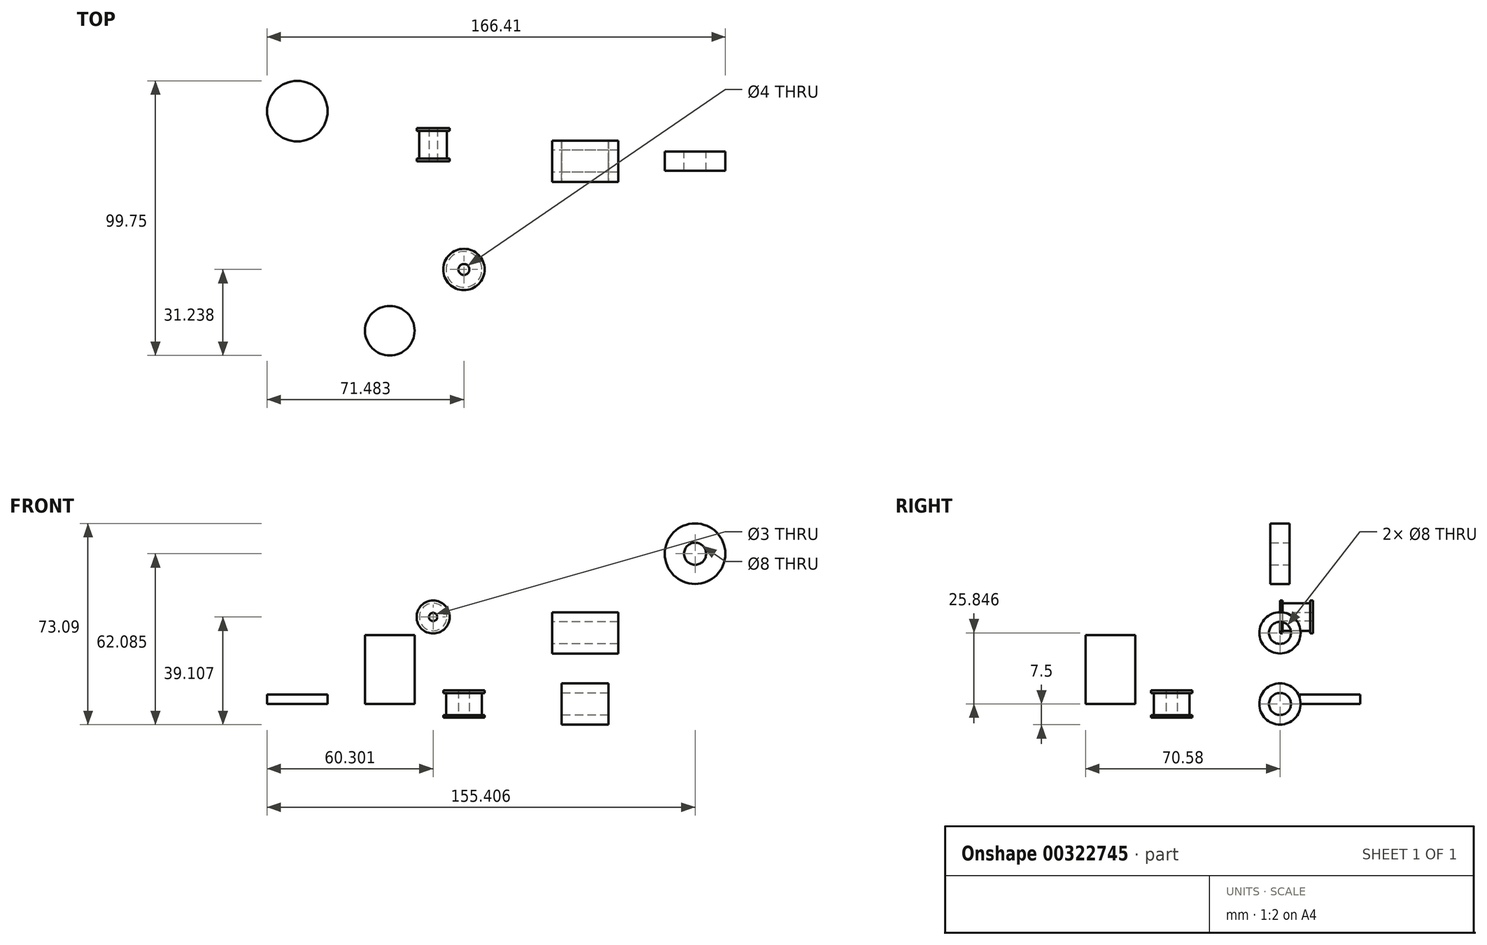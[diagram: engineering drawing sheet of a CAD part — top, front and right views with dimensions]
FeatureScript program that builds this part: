
annotation { "Feature Type Name" : "Feature", "Feature Type Description" : "" }
export const myFeature = defineFeature(function(context is Context, id is Id, definition is map)
    precondition{}
    {
        {
            var Q0;
            Q0=qCreatedBy(makeId("Right.planeOp"),FACE);
            var sketch = newSketch(context, id + "F0", { "sketchPlane" : qUnion([Q0])});
            skCircle(sketch, "E0", {"center": v(0, 0) * mm, "radius": 7.5 * mm});
            skCircle(sketch, "E1", {"center": v(0, 0) * mm, "radius": 4 * mm});
            skCircle(sketch, "E2", {"center": v(0, 25.85) * mm, "radius": 7.5 * mm});
            skCircle(sketch, "E3", {"center": v(0, 25.85) * mm, "radius": 4 * mm});
            skSolve(sketch);
        }
        {
            var Q0;
            Q0=makeQuery(id+"F0.imprint","IMPRINT",FACE,{"disambiguationData":[TD([[makeQuery(id+"F0.imprint","IMPRINT",EDGE,{"derivedFrom":sQuery(id+"F0.wireOp",EDGE,"E0")}),1.0]])]});
            extrude(context, id + "F1", {"entities" : qUnion([Q0]), "depth" : 17 * mm, "symmetric" : true});
        }
        {
            var Q0;
            Q0=makeQuery(id+"F0.imprint","IMPRINT",FACE,{"disambiguationData":[TD([[makeQuery(id+"F0.imprint","IMPRINT",EDGE,{"derivedFrom":sQuery(id+"F0.wireOp",EDGE,"E2")}),1.0]])]});
            extrude(context, id + "F2", {"entities" : qUnion([Q0]), "depth" : 24 * mm, "symmetric" : true});
        }
        {
            var Q0;
            Q0=qCreatedBy(makeId("Front.planeOp"),FACE);
            var sketch = newSketch(context, id + "F3", { "sketchPlane" : qUnion([Q0])});
            skCircle(sketch, "E4", {"center": v(-55.18, 31.6) * mm, "radius": 6 * mm});
            skCircle(sketch, "E5", {"center": v(-55.18, 31.6) * mm, "radius": 1.5 * mm});
            skSolve(sketch);
        }
        {
            var Q0;
            Q0=makeQuery(id+"F3.imprint","IMPRINT",FACE,{"disambiguationData":[TD([[makeQuery(id+"F3.imprint","IMPRINT",EDGE,{"derivedFrom":sQuery(id+"F3.wireOp",EDGE,"E4")}),1.0]])]});
            extrude(context, id + "F4", {"entities" : qUnion([Q0]), "oppositeDirection" : true, "depth" : 1 * mm});
        }
        {
            var Q0;
            Q0=makeQuery(id+"F4.opExtrude","CAP_FACE",FACE,{"disambiguationData":[OSD([sQuery(id+"F3.wireOp",EDGE,"E4"),sQuery(id+"F3.wireOp",EDGE,"E5")])],"isStart":false});
            var sketch = newSketch(context, id + "F5", { "sketchPlane" : qUnion([Q0])});
            skCircle(sketch, "E6", {"center": v(55.18, 31.6) * mm, "radius": 5 * mm});
            skSolve(sketch);
        }
        {
            var Q0;
            Q0=makeQuery(id+"F5.imprint","IMPRINT",FACE,{"disambiguationData":[TD([[makeQuery(id+"F5.imprint","IMPRINT",EDGE,{"derivedFrom":sQuery(id+"F5.wireOp",EDGE,"E6")}),1.0]])]});
            extrude(context, id + "F6", {"entities" : qUnion([Q0]), "operationType" : NewBodyOperationType.ADD, "depth" : 10 * mm});
        }
        {
            var Q0;
            Q0=makeQuery(id+"F6.opExtrude","CAP_FACE",FACE,{"disambiguationData":[OSD([sQuery(id+"F3.wireOp",EDGE,"E5"),sQuery(id+"F5.wireOp",EDGE,"E6")])],"isStart":false});
            var sketch = newSketch(context, id + "F7", { "sketchPlane" : qUnion([Q0])});
            skCircle(sketch, "E7", {"center": v(55.18, 31.6) * mm, "radius": 6 * mm});
            skSolve(sketch);
        }
        {
            var Q0;
            Q0=makeQuery(id+"F7.imprint","IMPRINT",FACE,{"disambiguationData":[TD([[makeQuery(id+"F7.imprint","IMPRINT",EDGE,{"derivedFrom":sQuery(id+"F7.wireOp",EDGE,"E7")}),1.0]])]});
            var Q1;
            Q1=makeQuery(id+"F7.imprint","IMPRINT",FACE,{"disambiguationData":[TD([[makeQuery(id+"F7.imprint","IMPRINT",EDGE,{"derivedFrom":makeQuery(id+"F6.opExtrude","CAP_EDGE",EDGE,{"disambiguationData":[OSD([sQuery(id+"F5.wireOp",EDGE,"E6")])],"isStart":false})}),1.0]])]});
            extrude(context, id + "F8", {"entities" : qUnion([Q0, Q1]), "operationType" : NewBodyOperationType.ADD, "depth" : 1 * mm});
        }
        {
            var Q0;
            Q0=qCreatedBy(makeId("Top.planeOp"),FACE);
            var sketch = newSketch(context, id + "F9", { "sketchPlane" : qUnion([Q0])});
            skCircle(sketch, "E8", {"center": v(-44, -39.34) * mm, "radius": 7.5 * mm});
            skCircle(sketch, "E9", {"center": v(-44, -39.34) * mm, "radius": 6.5 * mm});
            skCircle(sketch, "E10", {"center": v(-44, -39.34) * mm, "radius": 2 * mm});
            skSolve(sketch);
        }
        {
            var Q0;
            Q0=makeQuery(id+"F9.imprint","IMPRINT",FACE,{"disambiguationData":[TD([[makeQuery(id+"F9.imprint","IMPRINT",EDGE,{"derivedFrom":sQuery(id+"F9.wireOp",EDGE,"E9")}),1.0]])]});
            extrude(context, id + "F10", {"entities" : qUnion([Q0]), "depth" : 10 * mm, "symmetric" : true});
        }
        {
            var Q0;
            Q0=makeQuery(id+"F9.imprint","IMPRINT",FACE,{"disambiguationData":[TD([[makeQuery(id+"F9.imprint","IMPRINT",EDGE,{"derivedFrom":sQuery(id+"F9.wireOp",EDGE,"E8")}),1.0]])]});
            extrude(context, id + "F11", {"entities" : qUnion([Q0]), "operationType" : NewBodyOperationType.ADD, "depth" : 10 * mm, "symmetric" : true});
        }
        {
            var Q0;
            Q0=makeQuery(id+"F9.imprint","IMPRINT",FACE,{"disambiguationData":[TD([[makeQuery(id+"F9.imprint","IMPRINT",EDGE,{"derivedFrom":sQuery(id+"F9.wireOp",EDGE,"E8")}),1.0]])]});
            extrude(context, id + "F12", {"entities" : qUnion([Q0]), "operationType" : NewBodyOperationType.REMOVE, "oppositeDirection" : true, "depth" : 8 * mm, "symmetric" : true});
        }
        {
            var Q0;
            Q0=qCreatedBy(makeId("Front.planeOp"),FACE);
            var sketch = newSketch(context, id + "F13", { "sketchPlane" : qUnion([Q0])});
            skCircle(sketch, "E11", {"center": v(39.93, 54.59) * mm, "radius": 11 * mm});
            skCircle(sketch, "E12", {"center": v(39.93, 54.59) * mm, "radius": 4 * mm});
            skSolve(sketch);
        }
        {
            var Q0;
            Q0=makeQuery(id+"F13.imprint","IMPRINT",FACE,{"disambiguationData":[TD([[makeQuery(id+"F13.imprint","IMPRINT",EDGE,{"derivedFrom":sQuery(id+"F13.wireOp",EDGE,"E11")}),1.0]])]});
            extrude(context, id + "F14", {"entities" : qUnion([Q0]), "depth" : 7 * mm, "symmetric" : true});
        }
        {
            var Q0;
            Q0=qCreatedBy(makeId("Top.planeOp"),FACE);
            var sketch = newSketch(context, id + "F15", { "sketchPlane" : qUnion([Q0])});
            skCircle(sketch, "E13", {"center": v(-70.9, -61.58) * mm, "radius": 9 * mm});
            skSolve(sketch);
        }
        {
            var Q0;
            Q0=makeQuery(id+"F15.imprint","IMPRINT",FACE,{"disambiguationData":[TD([[makeQuery(id+"F15.imprint","IMPRINT",EDGE,{"derivedFrom":sQuery(id+"F15.wireOp",EDGE,"E13")}),1.0]])]});
            extrude(context, id + "F16", {"entities" : qUnion([Q0]), "depth" : 25 * mm, "offsetDistance" : 25 * mm});
        }
        {
            var Q0;
            Q0=qCreatedBy(makeId("Top.planeOp"),FACE);
            var sketch = newSketch(context, id + "F17", { "sketchPlane" : qUnion([Q0])});
            skCircle(sketch, "E14", {"center": v(-104.48, 18.17) * mm, "radius": 11 * mm});
            skSolve(sketch);
        }
        {
            var Q0;
            Q0=makeQuery(id+"F17.imprint","IMPRINT",FACE,{"disambiguationData":[TD([[makeQuery(id+"F17.imprint","IMPRINT",EDGE,{"derivedFrom":sQuery(id+"F17.wireOp",EDGE,"E14")}),1.0]])]});
            extrude(context, id + "F18", {"entities" : qUnion([Q0]), "depth" : 3.5 * mm, "offsetDistance" : 25 * mm});
        }
    });
